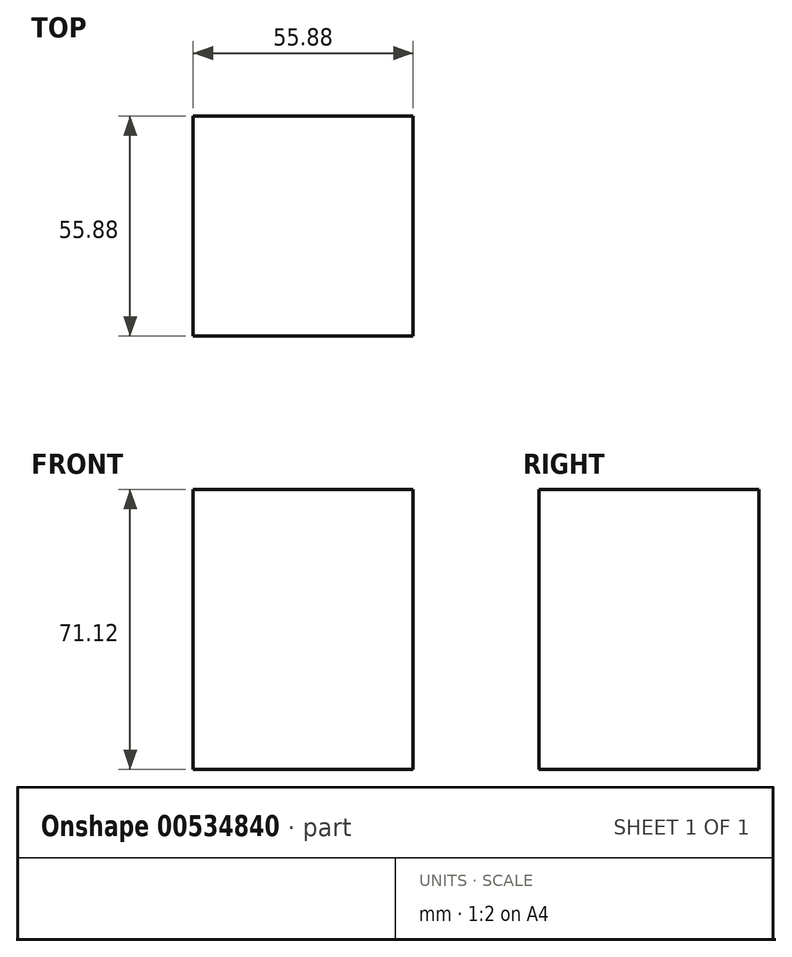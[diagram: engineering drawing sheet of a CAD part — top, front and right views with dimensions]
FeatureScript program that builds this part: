
annotation { "Feature Type Name" : "Feature", "Feature Type Description" : "" }
export const myFeature = defineFeature(function(context is Context, id is Id, definition is map)
    precondition{}
    {
        {
            var Q0;
            Q0=qCreatedBy(makeId("Top.planeOp"),FACE);
            var sketch = newSketch(context, id + "F0", { "sketchPlane" : qUnion([Q0])});
            skLineSegment(sketch, "E0.bottom", {"start": v(27.94, -27.94) * mm, "end": v(-27.94, -27.94) * mm});
            skLineSegment(sketch, "E0.top", {"start": v(27.94, 27.94) * mm, "end": v(-27.94, 27.94) * mm});
            skLineSegment(sketch, "E0.left", {"start": v(27.94, -27.94) * mm, "end": v(27.94, 27.94) * mm});
            skLineSegment(sketch, "E0.right", {"start": v(-27.94, -27.94) * mm, "end": v(-27.94, 27.94) * mm});
            skPoint(sketch, "E0.middle", {"position": v(0, 0) * mm});
            skSolve(sketch);
        }
        {
            var Q0;
            Q0=makeQuery(id+"F0.imprint","IMPRINT",FACE,{"disambiguationData":[TD([[makeQuery(id+"F0.imprint","IMPRINT",EDGE,{"derivedFrom":sQuery(id+"F0.wireOp",EDGE,"E0.bottom")}),-1.0]])]});
            extrude(context, id + "F1", {"entities" : qUnion([Q0]), "depth" : 71.12 * mm, "offsetDistance" : 25 * mm});
        }
    });
